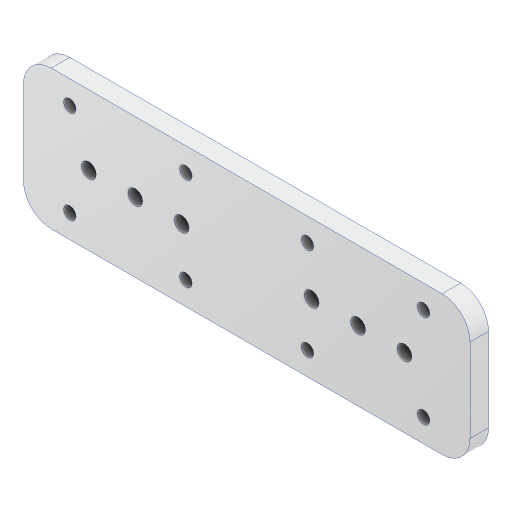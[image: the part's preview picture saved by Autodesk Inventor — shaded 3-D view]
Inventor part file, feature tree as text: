
AUTODESK INVENTOR PART (.ipt)
format: ipt  version: 2023.2 (Build 272271000, 271)  size: 175,616 bytes
history: native  units: mm
features: extrude x3, sketch x3, other x1, fillet x1, projected_geometry x1
ambient origin geometry x8: Origin, YZ Plane, XZ Plane, XY Plane, X Axis, Y Axis, Z Axis, Center Point
bodies: Body1 (feature_tree)
feature tree (9):
  other  "솔리드1"
  extrude  "돌출1"  Depth=96.2mm
  extrude  "돌출2"  Depth=30.0mm
  fillet  "모깎기1"  Radius=4.0mm
  extrude  "돌출3"  Depth=3.2mm
  sketch  "스케치1"
  sketch  "스케치2"
  sketch  "스케치3"
  projected_geometry  "투영된 루프1"
